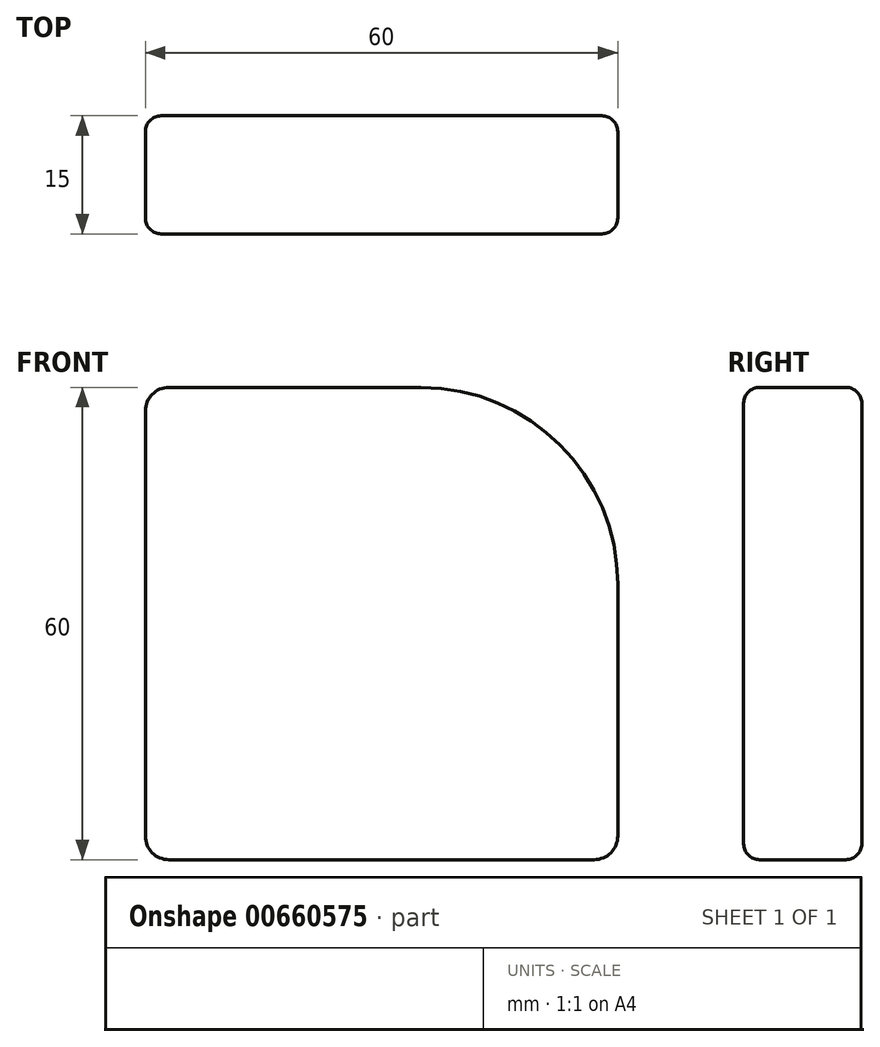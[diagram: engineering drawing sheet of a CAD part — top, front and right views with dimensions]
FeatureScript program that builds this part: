
annotation { "Feature Type Name" : "Feature", "Feature Type Description" : "" }
export const myFeature = defineFeature(function(context is Context, id is Id, definition is map)
    precondition{}
    {
        {
            var Q0;
            Q0=qCreatedBy(makeId("Front.planeOp"),FACE);
            var sketch = newSketch(context, id + "F0", { "sketchPlane" : qUnion([Q0])});
            skLineSegment(sketch, "E0.bottom", {"start": v(-3, 0) * mm, "end": v(-57, 0) * mm});
            skLineSegment(sketch, "E0.top", {"start": v(-25, 60) * mm, "end": v(-57, 60) * mm});
            skLineSegment(sketch, "E0.left", {"start": v(0, 3) * mm, "end": v(0, 35) * mm});
            skLineSegment(sketch, "E0.right", {"start": v(-60, 3) * mm, "end": v(-60, 57) * mm});
            skPoint(sketch, "E1.visualSharp", {"position": v(0, 60) * mm});
            skArc(sketch, "E1.filletArc", {"start": v(0, 35) * mm, "mid": v(-7.32, 52.68) * mm, "end": v(-25, 60) * mm});
            skPoint(sketch, "E2.visualSharp", {"position": v(-60, 60) * mm});
            skArc(sketch, "E2.filletArc", {"start": v(-57, 60) * mm, "mid": v(-59.12, 59.12) * mm, "end": v(-60, 57) * mm});
            skPoint(sketch, "E3.visualSharp", {"position": v(-60, 0) * mm});
            skArc(sketch, "E3.filletArc", {"start": v(-60, 3) * mm, "mid": v(-59.12, 0.88) * mm, "end": v(-57, 0) * mm});
            skPoint(sketch, "E4.visualSharp", {"position": v(0, 0) * mm});
            skArc(sketch, "E4.filletArc", {"start": v(-3, 0) * mm, "mid": v(-0.88, 0.88) * mm, "end": v(0, 3) * mm});
            skSolve(sketch);
        }
        {
            var Q0;
            Q0 = qSketchRegion(id + "F0", true);
            extrude(context, id + "F1", {"entities" : qUnion([Q0]), "depth" : 15 * mm, "offsetDistance" : 25 * mm});
        }
        {
            var Q0;
            Q0=makeQuery(id+"F1.opExtrude","CAP_FACE",FACE,{"disambiguationData":[OSD([sQuery(id+"F0.wireOp",EDGE,"E0.bottom"),sQuery(id+"F0.wireOp",EDGE,"E0.top"),sQuery(id+"F0.wireOp",EDGE,"E0.left"),sQuery(id+"F0.wireOp",EDGE,"E0.right"),sQuery(id+"F0.wireOp",EDGE,"E1.filletArc"),sQuery(id+"F0.wireOp",EDGE,"E2.filletArc"),sQuery(id+"F0.wireOp",EDGE,"E3.filletArc"),sQuery(id+"F0.wireOp",EDGE,"E4.filletArc")])],"isStart":false});
            fillet(context, id + "F2", {"entities" : qUnion([Q0]), "radius" : 2 * mm, "tangentPropagation" : true, "allowEdgeOverflow" : false});
        }
        {
            var Q0;
            Q0=makeQuery(id+"F1.opExtrude","CAP_EDGE",EDGE,{"disambiguationData":[OSD([sQuery(id+"F0.wireOp",EDGE,"E0.top")])],"isStart":true});
            fillet(context, id + "F3", {"entities" : qUnion([Q0]), "radius" : 2 * mm, "tangentPropagation" : true, "allowEdgeOverflow" : false});
        }
    });
